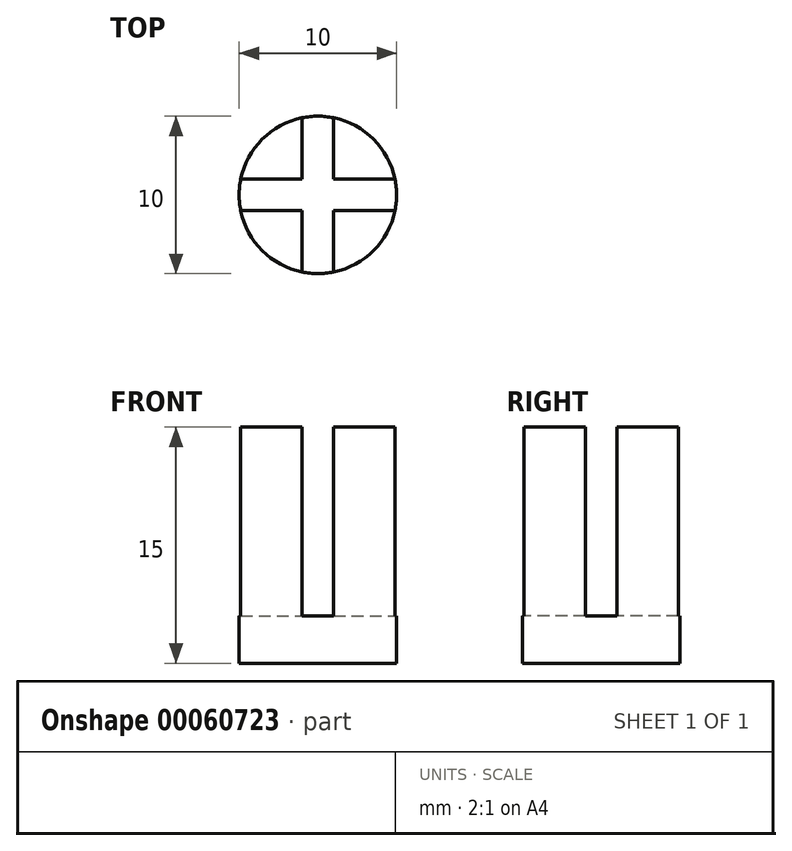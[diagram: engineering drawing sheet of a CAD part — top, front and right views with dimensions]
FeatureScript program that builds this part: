
annotation { "Feature Type Name" : "Feature", "Feature Type Description" : "" }
export const myFeature = defineFeature(function(context is Context, id is Id, definition is map)
    precondition{}
    {
        {
            var Q0;
            Q0=qCreatedBy(makeId("Top.planeOp"),FACE);
            var sketch = newSketch(context, id + "F0", { "sketchPlane" : qUnion([Q0])});
            skCircle(sketch, "E0", {"center": v(0, 0) * mm, "radius": 5 * mm});
            skSolve(sketch);
        }
        {
            var Q0;
            Q0=makeQuery(id+"F0.imprint","IMPRINT",FACE,{"disambiguationData":[TD([[makeQuery(id+"F0.imprint","IMPRINT",EDGE,{"derivedFrom":sQuery(id+"F0.wireOp",EDGE,"E0")}),1.0]])]});
            extrude(context, id + "F1", {"entities" : qUnion([Q0]), "depth" : 15 * mm});
        }
        {
            var Q0;
            Q0=makeQuery(id+"F1.opExtrude","CAP_FACE",FACE,{"disambiguationData":[OSD([sQuery(id+"F0.wireOp",EDGE,"E0")])],"isStart":false});
            var sketch = newSketch(context, id + "F2", { "sketchPlane" : qUnion([Q0])});
            skLineSegment(sketch, "E1.bottom", {"start": v(-1, 6.3) * mm, "end": v(1, 6.3) * mm});
            skLineSegment(sketch, "E1.top", {"start": v(-1, -8.35) * mm, "end": v(1, -8.35) * mm});
            skLineSegment(sketch, "E1.left", {"start": v(-1, 6.3) * mm, "end": v(-1, -8.35) * mm});
            skLineSegment(sketch, "E1.right", {"start": v(1, 6.3) * mm, "end": v(1, -8.35) * mm});
            skLineSegment(sketch, "E2.bottom", {"start": v(-6.38, 1) * mm, "end": v(10.5, 1) * mm});
            skLineSegment(sketch, "E2.top", {"start": v(-6.38, -1) * mm, "end": v(10.5, -1) * mm});
            skLineSegment(sketch, "E2.left", {"start": v(-6.38, 1) * mm, "end": v(-6.38, -1) * mm});
            skLineSegment(sketch, "E2.right", {"start": v(10.5, 1) * mm, "end": v(10.5, -1) * mm});
            skLineSegment(sketch, "E3", {"start": v(-10.5, 0) * mm, "end": v(16.65, 0) * mm, "construction": true});
            skLineSegment(sketch, "E4", {"start": v(0, 11.7) * mm, "end": v(0, -24.14) * mm, "construction": true});
            skSolve(sketch);
        }
        {
            var Q0;
            {var subQ0=sQuery(id+"F2.wireOp",EDGE,"E2.bottom");var subQ1=sQuery(id+"F2.wireOp",EDGE,"E1.left");var subQ2=makeQuery(id+"F2.imprint","INTERSECT",VERTEX,{"derivedFrom":[subQ1,subQ0]});Q0=makeQuery(id+"F2.imprint","IMPRINT",FACE,{"disambiguationData":[TD([[makeQuery(id+"F2.imprint","IMPRINT",EDGE,{"disambiguationData":[TD([[subQ2,-1.0]])],"derivedFrom":subQ1}),-1.0]])]});}
            var Q1;
            {var subQ0=sQuery(id+"F2.wireOp",EDGE,"E2.bottom");var subQ1=sQuery(id+"F2.wireOp",EDGE,"E1.left");var subQ2=makeQuery(id+"F2.imprint","INTERSECT",VERTEX,{"derivedFrom":[subQ1,subQ0]});Q1=makeQuery(id+"F2.imprint","IMPRINT",FACE,{"disambiguationData":[TD([[makeQuery(id+"F2.imprint","IMPRINT",EDGE,{"disambiguationData":[TD([[subQ2,-1.0]])],"derivedFrom":subQ1}),1.0]])]});}
            var Q2;
            {var subQ0=sQuery(id+"F2.wireOp",EDGE,"E2.bottom");var subQ1=sQuery(id+"F2.wireOp",EDGE,"E1.right");var subQ2=makeQuery(id+"F2.imprint","INTERSECT",VERTEX,{"derivedFrom":[subQ1,subQ0]});Q2=makeQuery(id+"F2.imprint","IMPRINT",FACE,{"disambiguationData":[TD([[makeQuery(id+"F2.imprint","IMPRINT",EDGE,{"disambiguationData":[TD([[subQ2,-1.0]])],"derivedFrom":subQ1}),1.0]])]});}
            var Q3;
            {var subQ0=sQuery(id+"F2.wireOp",EDGE,"E2.bottom");var subQ1=sQuery(id+"F2.wireOp",EDGE,"E1.left");var subQ2=makeQuery(id+"F2.imprint","INTERSECT",VERTEX,{"derivedFrom":[subQ1,subQ0]});Q3=makeQuery(id+"F2.imprint","IMPRINT",FACE,{"disambiguationData":[TD([[makeQuery(id+"F2.imprint","IMPRINT",EDGE,{"disambiguationData":[TD([[subQ2,1.0]])],"derivedFrom":subQ1}),1.0]])]});}
            var Q4;
            {var subQ0=sQuery(id+"F2.wireOp",EDGE,"E2.top");var subQ1=sQuery(id+"F2.wireOp",EDGE,"E1.left");var subQ2=makeQuery(id+"F2.imprint","INTERSECT",VERTEX,{"derivedFrom":[subQ1,subQ0]});Q4=makeQuery(id+"F2.imprint","IMPRINT",FACE,{"disambiguationData":[TD([[makeQuery(id+"F2.imprint","IMPRINT",EDGE,{"disambiguationData":[TD([[subQ2,-1.0]])],"derivedFrom":subQ1}),1.0]])]});}
            extrude(context, id + "F3", {"entities" : qUnion([Q0, Q1, Q2, Q3, Q4]), "operationType" : NewBodyOperationType.REMOVE, "oppositeDirection" : true, "depth" : 12 * mm});
        }
    });
